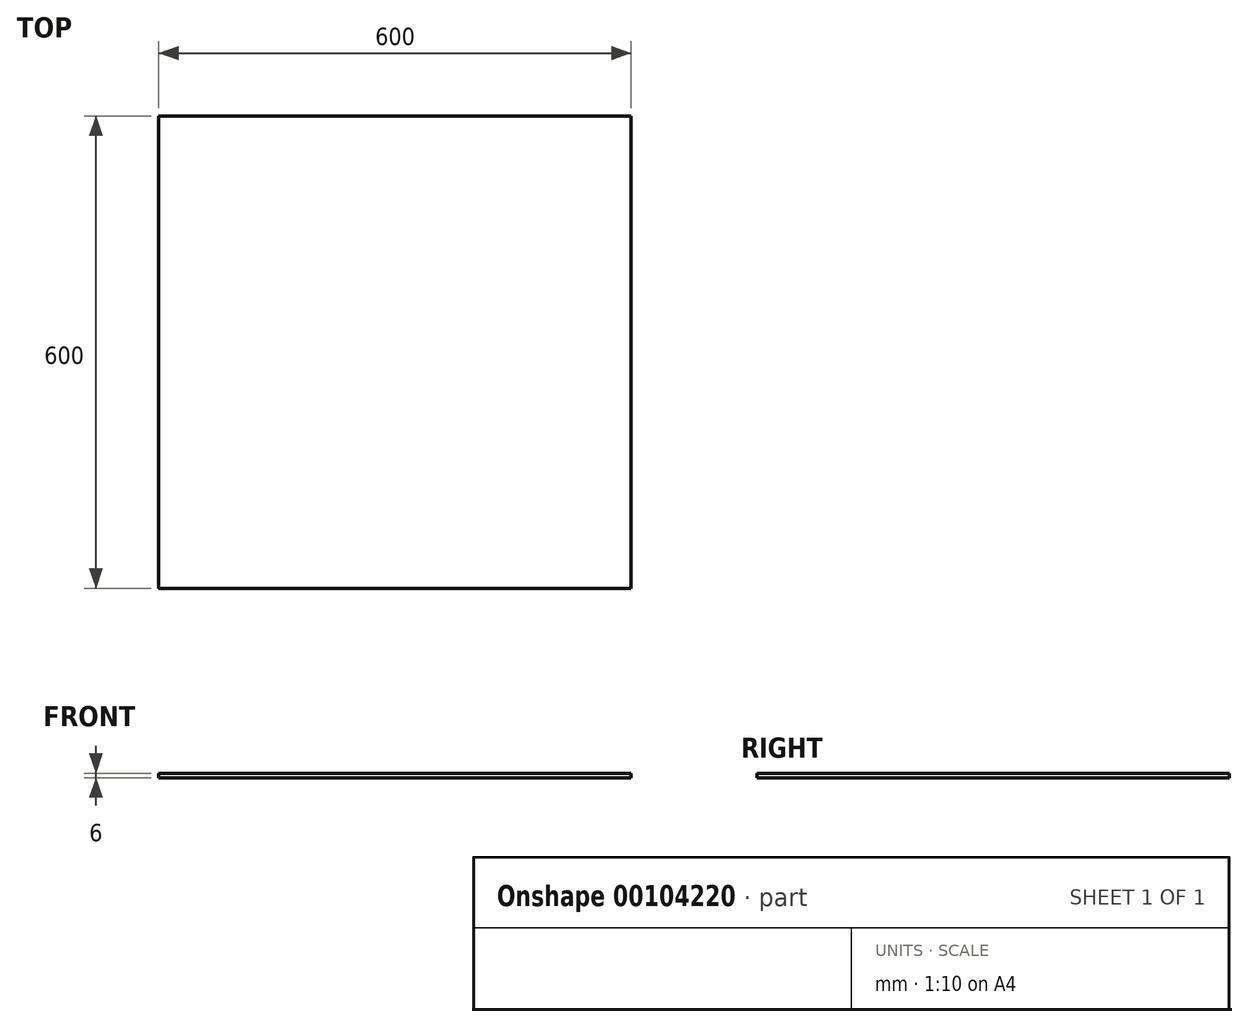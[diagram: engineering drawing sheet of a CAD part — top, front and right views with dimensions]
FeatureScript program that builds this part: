
annotation { "Feature Type Name" : "Feature", "Feature Type Description" : "" }
export const myFeature = defineFeature(function(context is Context, id is Id, definition is map)
    precondition{}
    {
        {
            var Q0;
            Q0=qCreatedBy(makeId("Top.planeOp"),FACE);
            var sketch = newSketch(context, id + "F0", { "sketchPlane" : qUnion([Q0])});
            skLineSegment(sketch, "E0.bottom", {"start": v(0, 0) * mm, "end": v(600, 0) * mm});
            skLineSegment(sketch, "E0.top", {"start": v(0, -600) * mm, "end": v(600, -600) * mm});
            skLineSegment(sketch, "E0.left", {"start": v(0, 0) * mm, "end": v(0, -600) * mm});
            skLineSegment(sketch, "E0.right", {"start": v(600, 0) * mm, "end": v(600, -600) * mm});
            skSolve(sketch);
        }
        {
            var Q0;
            Q0=makeQuery(id+"F0.imprint","IMPRINT",FACE,{"disambiguationData":[TD([[makeQuery(id+"F0.imprint","IMPRINT",EDGE,{"derivedFrom":sQuery(id+"F0.wireOp",EDGE,"E0.bottom")}),-1.0]])]});
            extrude(context, id + "F1", {"entities" : qUnion([Q0]), "depth" : 6 * mm});
        }
    });
